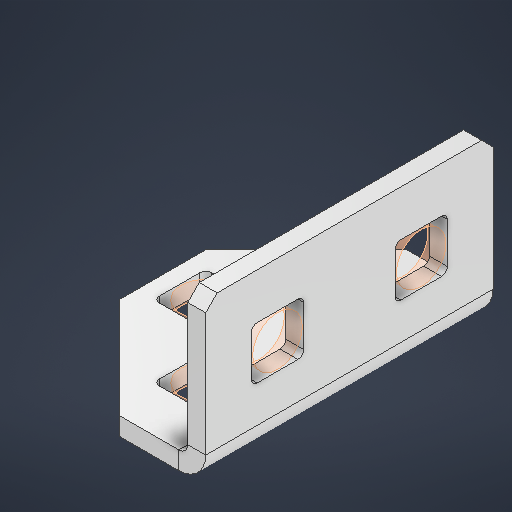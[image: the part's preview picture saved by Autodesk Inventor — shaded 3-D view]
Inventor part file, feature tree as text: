
AUTODESK INVENTOR PART (.ipt)
format: ipt  version: 2025.2 (Build 292293000, 293)  size: 501,760 bytes
history: native  units: in
note: dims shown in document units (in); Inventor stores cm internally (conversion verified against a paired STEP export)
features: other x16, sheet_metal_op x11, extrude x9, sketch x5, mirror x1, pattern_linear x1, chamfer x1
ambient origin geometry x8: Origin, YZ Plane, XZ Plane, XY Plane, X Axis, Y Axis, Z Axis, Center Point
bodies: Solid1 (feature_tree), Body (feature_tree)
feature tree (44):
  sheet_metal_op  "Flanges"
  other  "Flange Pattern Plane"
  other  "Flange Pattern Sketch"
  sheet_metal_op  "Flange Pattern"
  sheet_metal_op  "Body Pattern"
  other  "Arc Length"
  mirror  "Notch Mirror"
  pattern_linear  "Notch Pattern"  Spacing1=0.125in  [1 undecoded]
  chamfer  "End Chamfer"
  extrude  "Half Cut"  Depth=0.0625in
  extrude  "Extrusion2"  Depth=0.5in TaperAngle=90.0deg
  extrude  "Extrusion3"  Depth=0.25in
  other  "Plate1"
  sketch  "Sketch2"  dims[d1=1.0in]
  other  "Plate2"
  sheet_metal_op  "Bend1"
  sheet_metal_op  "Corner1"
  sketch  "Sketch Rectangular Pattern1"  dims[d0=1.0in]
  other  "Srf1"
  other  "Srf2"
  other  "Srf91"
  sheet_metal_op  "Body Pattern Sketch"
  sketch  "Sketch Rectangular Pattern2"  dims[d2=0.0625in]
  other  "Srf92"
  other  "Srf786"
  other  "Srf823"
  other  "Srf824"
  other  "Srf856"
  other  "Srf857"
  sketch  "Sketch17"  dims[d3=0.0625in]
  sketch  "Sketch18"  dims[d4=0.0312in d5=0.125in d6=0.0625in d7=0.5in d8=90.0deg d9=0.0312in d10=0.25in d11=0.0625in d12=0.0625in d16=0.182in d17=0.02in d18=0.0625in d19=0.0in d20=0.25in d21=0.25in d38=0.7874in d40=0.5in d41=0.7874in d43=1.0in d46=0.172in d47=1.0in d48=0.0in d49=0.182in d50=0.02in d51=0.25in d52=0.25in d53=0.0625in d54=0.0in d55=0.172in d56=1.0in d57=0.0in d58=0.25in d60=0.7874in d62=0.5in d63=0.7874in d65=0.5in d85=0.1473in d86=0.1782in d88=0.04in d89=0.0625in d90=0.0in d91=0.04in d92=0.0491in d95=2.5in d96=0.04in d97=0.25in d98=45.0deg d99=0.25in d100=0.5in d101=0.0in d102=2.497in d106=0.182in d107=0.02in d108=0.5in d109=0.5in d110=0.0625in d111=0.0in d112=0.172in d113=0.5in d114=0.0in d118=0.5in d119=0.5in d121=0.35in d122=0.0in d123=0.35in d124=0.35in d125=0.35in d126=0.35in d127=0.5in d128=0.0in]
  sheet_metal_op  "Flange Stamp"
  sheet_metal_op  "Flange Circle"
  sheet_metal_op  "Body Stamp"
  sheet_metal_op  "Body Circle"
  other  "Center Stamp"
  other  "Center Circle"
  sheet_metal_op  "Notch"
  extrude  "ExtrusionSrf2"  Depth=0.0625in
  extrude  "ExtrusionSrf92"  Depth=0.0625in
  extrude  "ExtrusionSrf823"  Depth=0.182in
  extrude  "ExtrusionSrf824"  Depth=0.02in
  extrude  "ExtrusionSrf856"  Depth=0.0625in
  extrude  "ExtrusionSrf857"  TaperAngle=0.0deg  [1 undecoded]
note: 2 required parameter values undecoded (feature->parameter linkage not recoverable at this tier; creation-order binding heuristic only, values carry confidence <= 0.55)
